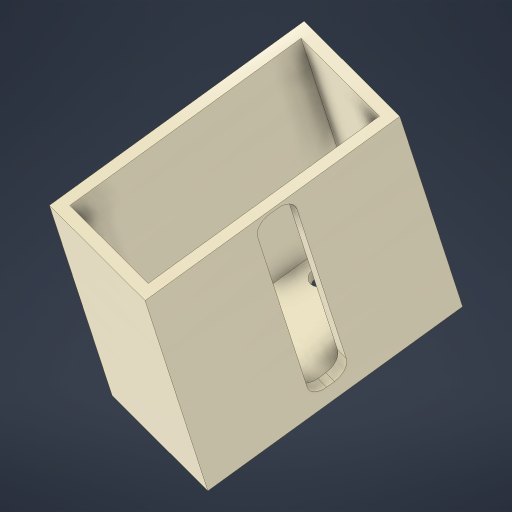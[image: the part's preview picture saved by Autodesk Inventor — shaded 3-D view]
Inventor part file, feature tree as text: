
AUTODESK INVENTOR PART (.ipt)
format: ipt  version: 2023 (Build 270158000, 158)  size: 231,424 bytes
history: native  units: mm
features: extrude x3, sketch x3, shell x1
ambient origin geometry x8: Origin, YZ Plane, XZ Plane, XY Plane, X Axis, Y Axis, Z Axis, Center Point
bodies: Solid1 (feature_tree)
feature tree (7):
  extrude  "Extrusion1"  Depth=33.0mm
  shell  "Shell1"  Thickness=66.0mm
  extrude  "Extrusion2"  Depth=10.0mm
  extrude  "Extrusion3"  Depth=5.0mm
  sketch  "Sketch1"  dims[d0=65.0mm d1=33.0mm d2=66.0mm d3=0.0mm]
  sketch  "Sketch2"  dims[d4=3.0mm d5=10.0mm]
  sketch  "Sketch3"  dims[d6=60.0mm d7=5.0mm d8=10.0mm d9=0.0mm d10=4.0mm d11=5.0mm d12=5.0mm d13=5.0mm d14=5.0mm d15=8.0mm d16=8.0mm d17=30.0mm d18=15.0mm d19=0.0mm d20=0.0mm]
